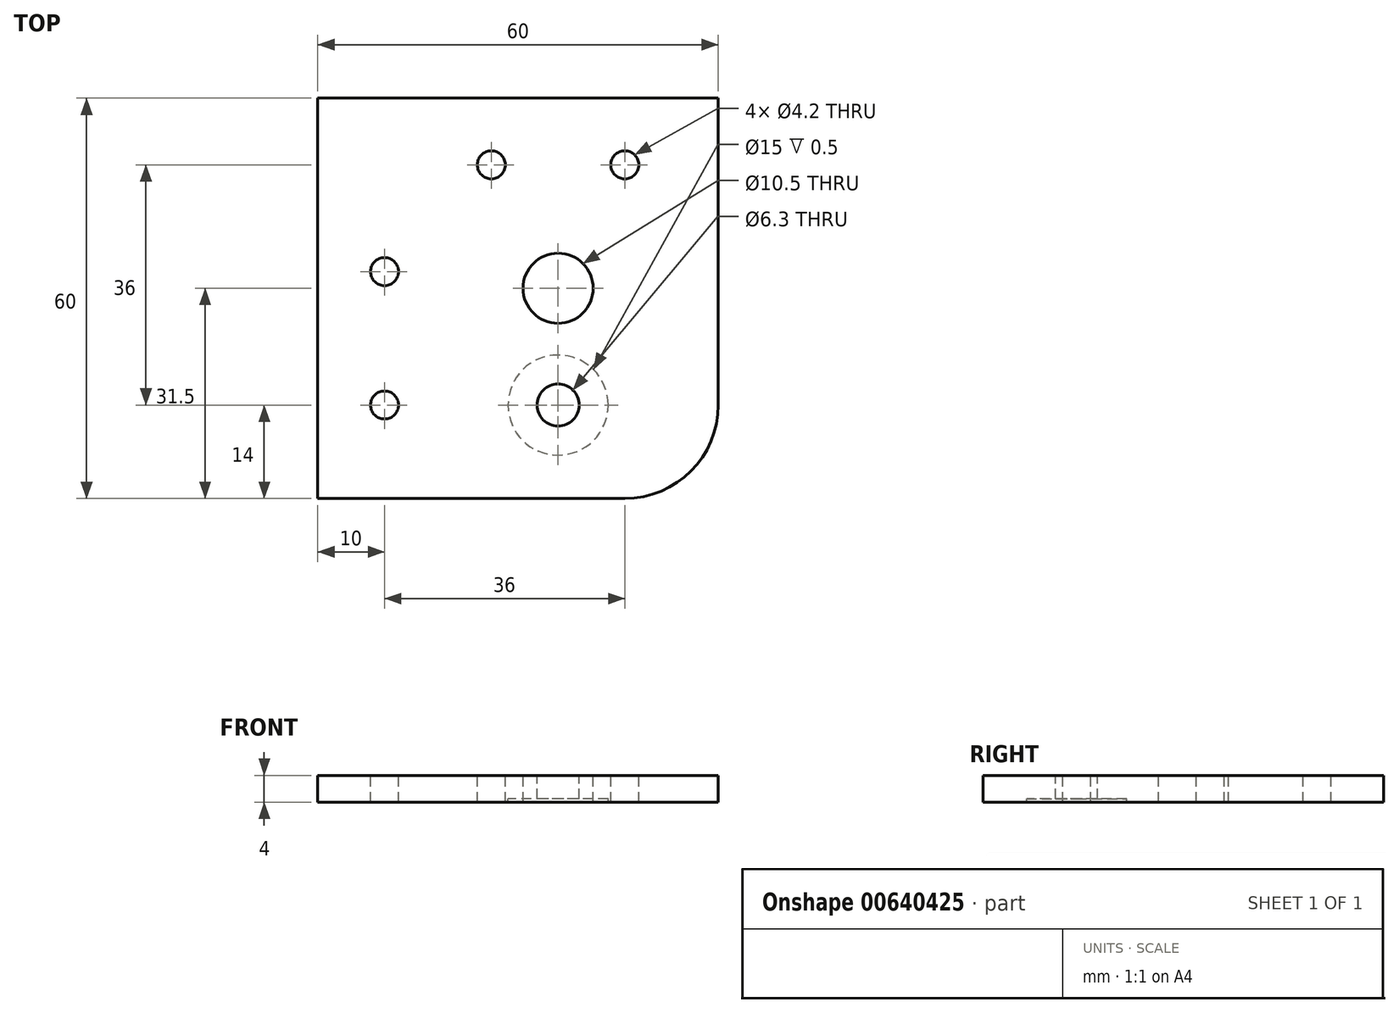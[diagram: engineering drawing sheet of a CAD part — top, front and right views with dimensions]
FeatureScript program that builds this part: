
annotation { "Feature Type Name" : "Feature", "Feature Type Description" : "" }
export const myFeature = defineFeature(function(context is Context, id is Id, definition is map)
    precondition{}
    {
        {
            var Q0;
            Q0=qCreatedBy(makeId("Top.planeOp"),FACE);
            var sketch = newSketch(context, id + "F0", { "sketchPlane" : qUnion([Q0])});
            skLineSegment(sketch, "E0.bottom", {"start": v(30, 30) * mm, "end": v(-30, 30) * mm});
            skLineSegment(sketch, "E0.top", {"start": v(16, -30) * mm, "end": v(-30, -30) * mm});
            skLineSegment(sketch, "E0.left", {"start": v(30, 30) * mm, "end": v(30, -16) * mm});
            skLineSegment(sketch, "E0.right", {"start": v(-30, 30) * mm, "end": v(-30, -30) * mm});
            skPoint(sketch, "E0.middle", {"position": v(0, 0) * mm});
            skLineSegment(sketch, "E1", {"start": v(-20, 39.63) * mm, "end": v(-20, -47.47) * mm, "construction": true});
            skLineSegment(sketch, "E2", {"start": v(-36.07, 20) * mm, "end": v(40.88, 20) * mm, "construction": true});
            skLineSegment(sketch, "E3", {"start": v(-34.57, 4) * mm, "end": v(40.88, 4) * mm, "construction": true});
            skLineSegment(sketch, "E4", {"start": v(-34.4, -16) * mm, "end": v(33.38, -16) * mm, "construction": true});
            skLineSegment(sketch, "E5", {"start": v(-4, 36.3) * mm, "end": v(-4, -34.48) * mm, "construction": true});
            skLineSegment(sketch, "E6", {"start": v(16, 35.64) * mm, "end": v(16, -33.15) * mm, "construction": true});
            skLineSegment(sketch, "E7", {"start": v(-33.51, 10) * mm, "end": v(33.1, 10) * mm, "construction": true});
            skLineSegment(sketch, "E8", {"start": v(-10, 32.52) * mm, "end": v(-10, -32.91) * mm, "construction": true});
            skCircle(sketch, "E9", {"center": v(-4, 20) * mm, "radius": 2.1 * mm});
            skCircle(sketch, "E10", {"center": v(16, 20) * mm, "radius": 2.1 * mm});
            skCircle(sketch, "E11", {"center": v(-20, 4) * mm, "radius": 2.1 * mm});
            skCircle(sketch, "E12", {"center": v(-20, -16) * mm, "radius": 2.1 * mm});
            skLineSegment(sketch, "E13", {"start": v(-34.42, 1.5) * mm, "end": v(36.86, 1.5) * mm, "construction": true});
            skLineSegment(sketch, "E14", {"start": v(6, 34.5) * mm, "end": v(6, -33.15) * mm, "construction": true});
            skCircle(sketch, "E15", {"center": v(6, 1.5) * mm, "radius": 5.25 * mm});
            skCircle(sketch, "E16", {"center": v(6, -16) * mm, "radius": 3.15 * mm});
            skArc(sketch, "E17", {"start": v(16, -30) * mm, "mid": v(25.9, -25.9) * mm, "end": v(30, -16) * mm});
            skPoint(sketch, "E18.orphan", {"position": v(30, -30) * mm});
            skCircle(sketch, "E19", {"center": v(6, -16) * mm, "radius": 7.5 * mm});
            skSolve(sketch);
        }
        {
            var Q0;
            Q0 = qSketchRegion(id + "F0", true);
            extrude(context, id + "F1", {"entities" : qUnion([Q0]), "oppositeDirection" : true, "depth" : 4 * mm, "offsetDistance" : 25 * mm});
        }
        {
            var Q0;
            Q0=makeQuery(id+"F0.imprint","IMPRINT",FACE,{"disambiguationData":[TD([[makeQuery(id+"F0.imprint","IMPRINT",EDGE,{"derivedFrom":sQuery(id+"F0.wireOp",EDGE,"E16")}),-1.0]])]});
            extrude(context, id + "F2", {"entities" : qUnion([Q0]), "operationType" : NewBodyOperationType.ADD, "oppositeDirection" : true, "depth" : 3.5 * mm, "offsetDistance" : 25 * mm});
        }
    });
